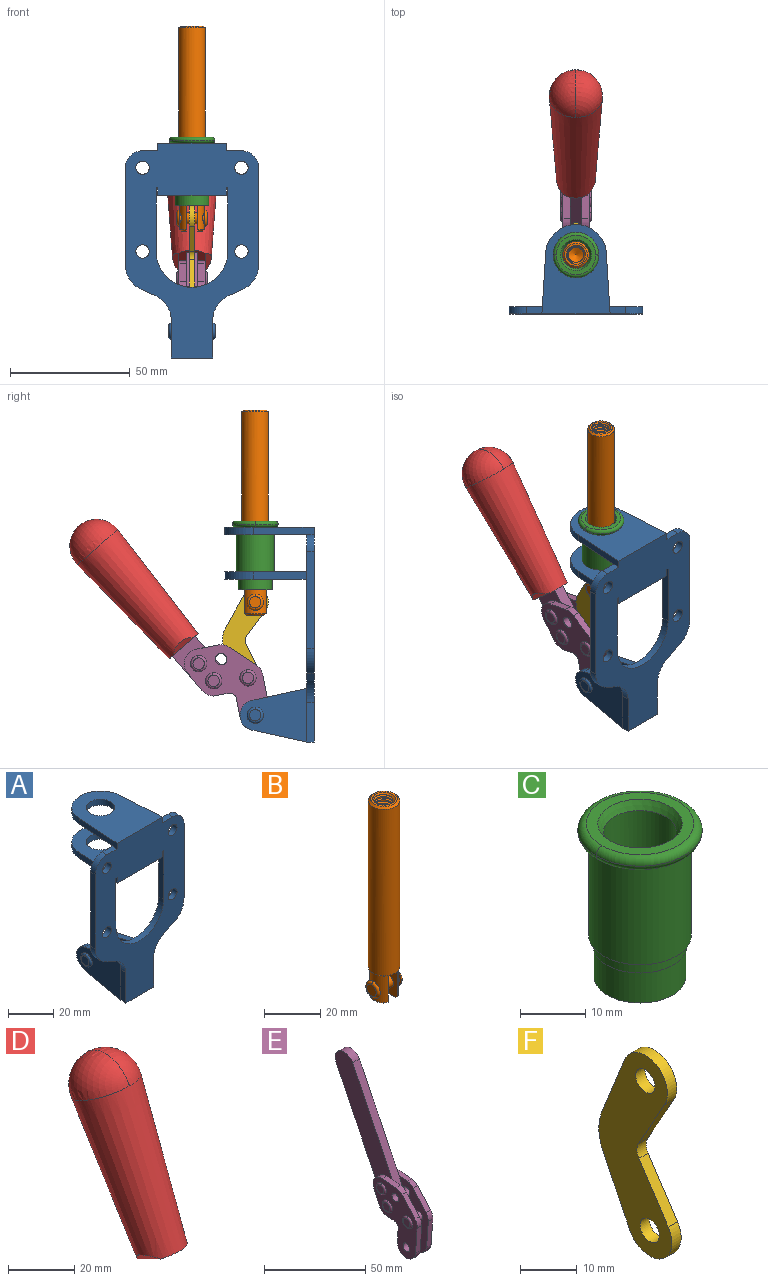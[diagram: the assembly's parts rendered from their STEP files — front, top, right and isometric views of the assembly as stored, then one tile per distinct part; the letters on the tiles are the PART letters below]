
ASSEMBLY  parts=6 mates=6
PART A: 55 faces, bbox 55.7x37.4x89.8 mm
  f0: torus R=2.41mm, axis (-1,0,0), area 15mm2, adj f11,f15,f25
  f1: torus R=2.41mm, axis (-1,0,0), area 15mm2, adj f10,f12,f22
  f2: cylinder r=2.78mm len=5.56mm, axis (0,-1,0), area 54.2mm2, adj f30,f54
  f3: cylinder r=14.99mm len=29.97mm, axis (0,-1,0), area 145.9mm2, adj f30,f49,f53,f54
  f4: cylinder r=2.78mm len=5.56mm, axis (0,-1,0), area 54.2mm2, adj f30,f54
  f5: cylinder r=2.78mm len=5.56mm, axis (0,-1,0), area 54.2mm2, adj f30,f54
  f6: cylinder r=2.78mm len=5.56mm, axis (0,-1,0), area 54.2mm2, adj f30,f54
  f7: cylinder r=6.35mm len=12.7mm, axis (0,0,1), area 123.6mm2, adj f27,f51
  f8: cylinder r=6.35mm len=12.7mm, axis (0,0,-1), area 124.7mm2, adj f21,f35
  f9: cylinder r=2.41mm len=11.18mm, axis (-1,0,0), area 169.4mm2, adj f16,f19
  f10: plane 4.83x4.83mm, normal (1,0,0), area 18.3mm2, adj f1,f12
  f11: plane 4.83x4.83mm, normal (-1,0,0), area 18.3mm2, adj f0,f15
  f12: torus R=2.41mm, axis (-1,0,0), area 15mm2, adj f1,f10,f22
  f13: cylinder r=6.35mm len=12.41mm, axis (1,0,0), area 53.4mm2, adj f18,f19,f22,f23
  f14: cylinder r=6.35mm len=12.41mm, axis (-1,0,0), area 53.4mm2, adj f16,f17,f24,f25
  f15: torus R=2.41mm, axis (-1,0,0), area 15mm2, adj f0,f11,f25
  f16: plane 27.86x22.35mm, normal (1,0,0), area 425.4mm2, adj f9,f14,f17,f24,f30
  f17: plane 22.86x4.97mm, normal (0,0.21,0.98), area 72.5mm2, adj f14,f16,f25,f30
  f18: plane 22.86x4.97mm, normal (0,0.21,0.98), area 72.5mm2, adj f13,f19,f22,f30
  f19: plane 27.86x22.35mm, normal (-1,0,0), area 425.4mm2, adj f9,f13,f18,f23,f30
  f20: cylinder r=12.7mm len=25.35mm, axis (0,0,-1), area 119.8mm2, adj f21,f34,f35,f36
  f21: plane 34.21x28.07mm, normal (0,0,-1), area 702.4mm2, adj f8,f20,f30,f34,f36
  f22: plane 27.96x22.45mm, normal (1,0,0), area 407.2mm2, adj f1,f12,f13,f18,f23,f30,f42,f43
  f23: plane 22.86x4.97mm, normal (0,0.21,-0.98), area 72.5mm2, adj f13,f19,f22,f44
  f24: plane 22.86x4.97mm, normal (0,0.21,-0.98), area 72.5mm2, adj f14,f16,f25,f44
  f25: plane 27.86x22.35mm, normal (-1,0,0), area 407.1mm2, adj f0,f14,f15,f17,f24,f30,f45,f46
  f26: plane 3.1x0.95mm, normal (0,0,-1), area 2.7mm2, adj f30,f49,f50,f54
  f27: plane 34.21x28.07mm, normal (0,0,1), area 702.4mm2, adj f7,f28,f30,f50,f52
  f28: cylinder r=12.7mm len=25.35mm, axis (0,0,1), area 118.8mm2, adj f27,f50,f51,f52
  f29: plane 3.1x0.95mm, normal (0,0,-1), area 2.7mm2, adj f30,f52,f53,f54
  f30: plane 86.54x55.63mm, normal (0,1,0), area 2362.9mm2, adj f2,f3,f4,f5,f6,f16,f17,f18
  f31: plane 40.56x3.1mm, normal (-1,0,0), area 125.7mm2, adj f30,f32,f48,f54
  f32: cylinder r=7.11mm len=7.11mm, axis (0,-1,0), area 34.6mm2, adj f30,f31,f33,f54
  f33: plane 6.67x3.1mm, normal (0,0,1), area 20.4mm2, adj f30,f32,f34,f54
  f34: plane 25.39x3.13mm, normal (-1,0.06,0), area 79.5mm2, adj f20,f21,f33,f35,f54
  f35: plane 37.31x28.45mm, normal (0,0,1), area 789.9mm2, adj f8,f20,f34,f36,f54
  f36: plane 25.39x3.13mm, normal (1,0.06,0), area 79.5mm2, adj f20,f21,f35,f37,f54
  f37: plane 6.67x3.1mm, normal (0,0,1), area 20.4mm2, adj f30,f36,f38,f54
  f38: cylinder r=7.11mm len=7.11mm, axis (0,-1,0), area 34.6mm2, adj f30,f37,f39,f54
  f39: plane 40.56x3.1mm, normal (1,0,0), area 125.7mm2, adj f30,f38,f40,f54
  f40: cylinder r=11.18mm len=10.16mm, axis (0,-1,0), area 39.5mm2, adj f30,f39,f41,f54
  f41: plane 6.09x3.1mm, normal (0.42,0,-0.91), area 20.8mm2, adj f30,f40,f42,f54
  f42: cylinder r=11.18mm len=9.41mm, axis (0,-1,0), area 37.2mm2, adj f22,f30,f41,f43,f54
  f43: plane 16.5x3.1mm, normal (1,0,0), area 51.1mm2, adj f22,f42,f44,f54
  f44: plane 17.37x3.1mm, normal (0,0,-1), area 53.8mm2, adj f23,f24,f30,f43,f45,f54
  f45: plane 16.5x3.1mm, normal (-1,0,0), area 51.1mm2, adj f25,f44,f46,f54
  f46: cylinder r=11.18mm len=9.41mm, axis (0,-1,0), area 37.2mm2, adj f25,f30,f45,f47,f54
  f47: plane 6.09x3.1mm, normal (-0.42,0,-0.91), area 20.8mm2, adj f30,f46,f48,f54
  f48: cylinder r=11.18mm len=10.16mm, axis (0,-1,0), area 39.5mm2, adj f30,f31,f47,f54
  f49: plane 26.54x3.1mm, normal (-1,0,0), area 82.3mm2, adj f3,f26,f30,f54
  f50: plane 25.39x3.1mm, normal (1,0.06,0), area 78.8mm2, adj f26,f27,f28,f51,f54
  f51: plane 37.31x28.45mm, normal (0,0,-1), area 789.9mm2, adj f7,f28,f50,f52,f54
  f52: plane 25.39x3.1mm, normal (-1,0.06,0), area 78.8mm2, adj f27,f28,f29,f51,f54
  f53: plane 26.54x3.1mm, normal (1,0,0), area 82.3mm2, adj f3,f29,f30,f54
  f54: plane 89.66x55.63mm, normal (0,-1,0), area 2678.5mm2, adj f2,f3,f4,f5,f6,f26,f29,f31
PART B: 48 faces, bbox 12.6x11.1x86.1 mm
  f0: torus R=2.41mm, axis (-1,0,0), area 15mm2, adj f30,f32,f34
  f1: torus R=2.41mm, axis (-1,0,0), area 15mm2, adj f29,f31,f33
  f2: cylinder r=5.54mm len=72.39mm, axis (0,0,1), area 2518.5mm2, adj f3,f4,f42,f43
  f3: cone r=5.54mm half-angle=45deg, axis (0,0,1), area 7.6mm2, adj f2,f5,f41
  f4: cone r=5.54mm half-angle=45deg, axis (0,0,-1), area 34.9mm2, adj f2,f39
  f5: cylinder r=5.08mm len=11.48mm, axis (0,0,1), area 108.3mm2, adj f3,f7,f8,f41
  f6: cylinder r=2.41mm len=4.83mm, axis (-1,0,0), area 71.2mm2, adj f40,f41
  f7: cylinder r=2.41mm len=4.83mm, axis (-1,0,0), area 7.6mm2, adj f5,f34
  f8: cone r=5.08mm half-angle=45deg, axis (0,0,1), area 10.6mm2, adj f5,f37,f41
  f9: cone r=3.98mm half-angle=45deg, axis (0,0,1), area 17.6mm2, adj f27,f39,f45,f46,f47
  f10: cylinder r=2.41mm len=4.83mm, axis (-1,0,0), area 7.6mm2, adj f33,f38
  f11: cylinder r=3.2mm len=6.4mm, axis (0,0,1), area 78.4mm2, adj f12,f28,f44,f45,f47
  f12: cylinder r=3.2mm len=6.4mm, axis (0,0,1), area 10.5mm2, adj f11,f13,f45,f47
  f13: cylinder r=3.2mm len=6.4mm, axis (0,0,1), area 10.5mm2, adj f12,f14,f45,f47
  f14: cylinder r=3.2mm len=6.4mm, axis (0,0,1), area 10.5mm2, adj f13,f15,f45,f47
  f15: cylinder r=3.2mm len=6.4mm, axis (0,0,1), area 10.5mm2, adj f14,f16,f45,f47
  f16: cylinder r=3.2mm len=6.4mm, axis (0,0,1), area 10.5mm2, adj f15,f17,f45,f47
  f17: cylinder r=3.2mm len=6.4mm, axis (0,0,1), area 10.5mm2, adj f16,f18,f45,f47
  f18: cylinder r=3.2mm len=6.4mm, axis (0,0,1), area 10.5mm2, adj f17,f19,f45,f47
  f19: cylinder r=3.2mm len=6.4mm, axis (0,0,1), area 10.5mm2, adj f18,f20,f45,f47
  f20: cylinder r=3.2mm len=6.4mm, axis (0,0,1), area 10.5mm2, adj f19,f21,f45,f47
  f21: cylinder r=3.2mm len=6.4mm, axis (0,0,1), area 10.5mm2, adj f20,f22,f45,f47
  f22: cylinder r=3.2mm len=6.4mm, axis (0,0,1), area 10.5mm2, adj f21,f23,f45,f47
  f23: cylinder r=3.2mm len=6.4mm, axis (0,0,1), area 10.5mm2, adj f22,f24,f45,f47
  f24: cylinder r=3.2mm len=6.4mm, axis (0,0,1), area 10.5mm2, adj f23,f25,f45,f47
  f25: cylinder r=3.2mm len=6.4mm, axis (0,0,1), area 10.5mm2, adj f24,f26,f45,f47
  f26: cylinder r=3.2mm len=6.4mm, axis (0,0,1), area 10.5mm2, adj f25,f27,f45,f47
  f27: cylinder r=3.2mm len=6.4mm, axis (0,0,1), area 7.4mm2, adj f9,f26,f45,f47
  f28: cone r=3.2mm half-angle=60deg, axis (0,0,1), area 37.2mm2, adj f11
  f29: plane 4.83x4.83mm, normal (-1,0,0), area 18.3mm2, adj f1,f31
  f30: plane 4.83x4.83mm, normal (1,0,0), area 18.3mm2, adj f0,f32
  f31: torus R=2.41mm, axis (-1,0,0), area 15mm2, adj f1,f29,f33
  f32: torus R=2.41mm, axis (-1,0,0), area 15mm2, adj f0,f30,f34
  f33: plane 6.83x6.83mm, normal (1,0,0), area 18.3mm2, adj f1,f10,f31
  f34: plane 6.83x6.83mm, normal (-1,0,0), area 18.3mm2, adj f0,f7,f32
  f35: cone r=5.08mm half-angle=45deg, axis (0,0,1), area 10.6mm2, adj f36,f38,f40
  f36: plane 7.25x1.97mm, normal (0,0,-1), area 10mm2, adj f35,f40
  f37: plane 7.25x1.97mm, normal (0,0,-1), area 10mm2, adj f8,f41
  f38: cylinder r=5.08mm len=11.48mm, axis (0,0,1), area 108.3mm2, adj f10,f35,f40,f42
  f39: plane 9.55x9.55mm, normal (0,0,1), area 22mm2, adj f4,f9
  f40: plane 12.76x10.09mm, normal (1,0,0), area 95.7mm2, adj f6,f35,f36,f38,f42,f43
  f41: plane 12.76x10.09mm, normal (-1,0,0), area 95.7mm2, adj f3,f5,f6,f8,f37,f43
  f42: cone r=5.54mm half-angle=45deg, axis (0,0,1), area 7.6mm2, adj f2,f38,f40
  f43: plane 11.07x4.7mm, normal (0,0,-1), area 50.4mm2, adj f2,f40,f41
  f44: plane 0.89x0.62mm, normal (-1,0,0), area 0.3mm2, adj f11,f45,f46,f47
  f45: bspline ~24.8x7.63mm, area 266.6mm2, adj f9,f11,f12,f13,f14,f15,f16,f17
  f46: bspline ~24.87x7.63mm, area 73.6mm2, adj f9,f44,f45,f47
  f47: bspline ~24.98x7.63mm, area 272.5mm2, adj f9,f11,f12,f13,f14,f15,f16,f17
PART C: 15 faces, bbox 20.6x20.6x28.7 mm
  f0: torus R=8.26mm, axis (0,0,1), area 56.8mm2, adj f1,f10,f12
  f1: torus R=8.26mm, axis (0,0,1), area 56.8mm2, adj f0,f6,f13
  f2: cylinder r=5.59mm len=25.91mm, axis (0,0,1), area 909.6mm2, adj f3,f4
  f3: cone r=6.86mm half-angle=45deg, axis (0,0,-1), area 70.2mm2, adj f2,f14
  f4: cone r=6.47mm half-angle=30deg, axis (0,0,1), area 66.7mm2, adj f2,f13
  f5: cylinder r=7.04mm len=14.07mm, axis (0,0,1), area 252.6mm2, adj f11,f14
  f6: torus R=8.26mm, axis (0,0,1), area 56.8mm2, adj f1,f12,f13
  f7: cylinder r=7.16mm len=14.33mm, axis (0,0,1), area 91.5mm2, adj f9,f11
  f8: cylinder r=7.86mm len=18.42mm, axis (0,0,1), area 909.6mm2, adj f9,f10
  f9: plane 15.72x15.72mm, normal (0,0,-1), area 33mm2, adj f7,f8
  f10: plane 16.51x16.51mm, normal (0,0,-1), area 19.9mm2, adj f0,f8,f12
  f11: plane 14.33x14.33mm, normal (0,0,-1), area 5.7mm2, adj f5,f7
  f12: torus R=8.26mm, axis (0,0,1), area 56.8mm2, adj f0,f6,f10
  f13: plane 16.51x16.51mm, normal (0,0,1), area 82.7mm2, adj f1,f4,f6
  f14: plane 14.07x14.07mm, normal (0,0,-1), area 7.8mm2, adj f3,f5
PART D: 11 faces, bbox 22.3x42.6x64.5 mm
  f0: sphere r=11.13mm, area 411.4mm2, adj f1,f8
  f1: cone r=11.11mm half-angle=3.3deg, axis (0,0.44,0.9), area 3251.8mm2, adj f0,f7,f8,f9,f10
  f2: cylinder r=6.16mm len=11.7mm, axis (1,0,0), area 89.5mm2, adj f3,f4,f5,f6
  f3: plane 60.23x36.75mm, normal (-1,0,0), area 763.6mm2, adj f2,f4,f6,f10
  f4: plane 51.37x25.05mm, normal (0,0.9,-0.44), area 264.2mm2, adj f2,f3,f5,f10
  f5: plane 60.23x36.75mm, normal (1,0,0), area 763.6mm2, adj f2,f4,f6,f10
  f6: plane 51.37x25.05mm, normal (0,-0.9,0.44), area 264.2mm2, adj f2,f3,f5,f10
  f7: plane 9.95x5.95mm, normal (0.71,-0.31,-0.64), area 25.8mm2, adj f1,f10
  f8: sphere r=11.13mm, area 411.4mm2, adj f0,f1
  f9: plane 9.95x5.95mm, normal (-0.71,-0.31,-0.64), area 25.8mm2, adj f1,f10
  f10: plane 14.27x11.38mm, normal (0,-0.44,-0.9), area 106.7mm2, adj f1,f3,f4,f5,f6,f7,f9
PART E: 59 faces, bbox 12.9x60.2x99.6 mm
  f0: torus R=2.39mm, axis (-1,0,0), area 14.9mm2, adj f20,f43,f51
  f1: torus R=2.39mm, axis (-1,0,0), area 14.9mm2, adj f19,f42,f51
  f2: torus R=2.39mm, axis (-1,0,0), area 14.9mm2, adj f18,f35,f51
  f3: torus R=2.39mm, axis (-1,0,0), area 14.9mm2, adj f14,f17,f23
  f4: torus R=2.39mm, axis (-1,0,0), area 14.9mm2, adj f13,f16,f23
  f5: torus R=2.39mm, axis (-1,0,0), area 14.9mm2, adj f12,f15,f23
  f6: cylinder r=2.39mm len=4.78mm, axis (1,0,0), area 46.5mm2, adj f48,f50,f51
  f7: cylinder r=2.39mm len=4.78mm, axis (1,0,0), area 46.5mm2, adj f50,f51
  f8: cylinder r=6.35mm len=12.68mm, axis (1,0,0), area 61.8mm2, adj f38,f39,f50,f51
  f9: cylinder r=2.39mm len=4.78mm, axis (-1,0,0), area 70.5mm2, adj f46,f50
  f10: cylinder r=2.39mm len=4.78mm, axis (-1,0,0), area 46.5mm2, adj f23,f45,f46
  f11: cylinder r=2.39mm len=4.78mm, axis (-1,0,0), area 46.5mm2, adj f23,f46
  f12: plane 4.78x4.78mm, normal (1,0,0), area 17.9mm2, adj f5,f15
  f13: plane 4.78x4.78mm, normal (1,0,0), area 17.9mm2, adj f4,f16
  f14: plane 4.78x4.78mm, normal (1,0,0), area 17.9mm2, adj f3,f17
  f15: torus R=2.39mm, axis (-1,0,0), area 14.9mm2, adj f5,f12,f23
  f16: torus R=2.39mm, axis (-1,0,0), area 14.9mm2, adj f4,f13,f23
  f17: torus R=2.39mm, axis (-1,0,0), area 14.9mm2, adj f3,f14,f23
  f18: plane 4.78x4.78mm, normal (-1,0,0), area 17.9mm2, adj f2,f35
  f19: plane 4.78x4.78mm, normal (-1,0,0), area 17.9mm2, adj f1,f42
  f20: plane 4.78x4.78mm, normal (-1,0,0), area 17.9mm2, adj f0,f43
  f21: plane 2.26x0.2mm, normal (1,0,0), area 0.2mm2, adj f31,f44
  f22: plane 2.26x0.2mm, normal (-1,0,0), area 0.2mm2, adj f41,f44
  f23: plane 39.37x30.77mm, normal (1,0,0), area 565.5mm2, adj f3,f4,f5,f10,f11,f15,f16,f17
  f24: cylinder r=6.1mm len=4.15mm, axis (-1,0,0), area 14.7mm2, adj f23,f25,f32,f46
  f25: plane 10.25x9.01mm, normal (0,-0.75,0.66), area 42.3mm2, adj f23,f24,f26,f46
  f26: cylinder r=6.35mm len=4.64mm, axis (-1,0,0), area 15.6mm2, adj f23,f25,f27,f46
  f27: plane 15.84x3.1mm, normal (0,-1,-0.07), area 49.2mm2, adj f23,f26,f28,f46
  f28: cylinder r=6.35mm len=12.68mm, axis (-1,0,0), area 61.8mm2, adj f23,f27,f29,f46
  f29: plane 8.11x3.1mm, normal (0,1,0.07), area 25.2mm2, adj f23,f28,f30,f46
  f30: cylinder r=3.05mm len=3.25mm, axis (-1,0,0), area 14.8mm2, adj f23,f29,f31,f46
  f31: plane 5.99x3.1mm, normal (0,0.07,-1), area 18.6mm2, adj f21,f23,f30,f44,f46
  f32: plane 9.5x3.1mm, normal (0,-0.07,1), area 29.5mm2, adj f23,f24,f33,f46,f47
  f33: cylinder r=6.1mm len=8.63mm, axis (-1,0,0), area 39.1mm2, adj f23,f32,f34,f47
  f34: plane 8.65x3.96mm, normal (0,0.91,-0.42), area 29.5mm2, adj f23,f33,f44,f47
  f35: torus R=2.39mm, axis (-1,0,0), area 14.9mm2, adj f2,f18,f51
  f36: plane 10.25x9.01mm, normal (0,-0.75,0.66), area 42.3mm2, adj f37,f49,f50,f51
  f37: cylinder r=6.35mm len=4.64mm, axis (1,0,0), area 15.6mm2, adj f36,f38,f50,f51
  f38: plane 15.84x3.1mm, normal (0,-1,-0.07), area 49.2mm2, adj f8,f37,f50,f51
  f39: plane 8.11x3.1mm, normal (0,1,0.07), area 25.2mm2, adj f8,f40,f50,f51
  f40: cylinder r=3.05mm len=3.25mm, axis (1,0,0), area 14.8mm2, adj f39,f41,f50,f51
  f41: plane 5.99x3.1mm, normal (0,0.07,-1), area 18.6mm2, adj f22,f40,f44,f50,f51
  f42: torus R=2.39mm, axis (-1,0,0), area 14.9mm2, adj f1,f19,f51
  f43: torus R=2.39mm, axis (-1,0,0), area 14.9mm2, adj f0,f20,f51
  f44: cylinder r=6.35mm len=12.12mm, axis (-1,0,0), area 128.9mm2, adj f21,f22,f23,f31,f34,f41,f46,f47
  f45: plane 2.65x1.35mm, normal (1,0,0), area 1mm2, adj f10,f55
  f46: plane 39.08x20.42mm, normal (-1,0,0), area 412.5mm2, adj f9,f10,f11,f24,f25,f26,f27,f28
  f47: plane 77.62x39.82mm, normal (1,0,0), area 850mm2, adj f32,f33,f34,f44,f53,f54,f55
  f48: plane 2.65x1.35mm, normal (-1,0,0), area 1mm2, adj f6,f55
  f49: cylinder r=6.1mm len=4.15mm, axis (1,0,0), area 14.7mm2, adj f36,f50,f51,f56
  f50: plane 39.08x20.42mm, normal (1,0,0), area 412.5mm2, adj f6,f7,f8,f9,f36,f37,f38,f39
  f51: plane 39.37x30.77mm, normal (-1,0,0), area 565.5mm2, adj f0,f1,f2,f6,f7,f8,f35,f36
  f52: plane 8.65x3.96mm, normal (0,0.91,-0.42), area 29.5mm2, adj f44,f51,f57,f58
  f53: plane 68.49x33.4mm, normal (0,0.9,-0.44), area 358.1mm2, adj f44,f47,f54,f58
  f54: cylinder r=6.35mm len=12.06mm, axis (1,0,0), area 93.7mm2, adj f47,f53,f55,f58
  f55: plane 68.49x33.4mm, normal (0,-0.9,0.44), area 358.1mm2, adj f44,f45,f46,f47,f48,f50,f54,f58
  f56: plane 9.5x3.1mm, normal (0,-0.07,1), area 29.5mm2, adj f49,f50,f51,f57,f58
  f57: cylinder r=6.1mm len=8.63mm, axis (1,0,0), area 39.1mm2, adj f51,f52,f56,f58
  f58: plane 77.62x39.82mm, normal (-1,0,0), area 850mm2, adj f44,f52,f53,f54,f55,f56,f57
PART F: 12 faces, bbox 2.3x18.2x42.8 mm
  f0: cylinder r=2.4mm len=4.8mm, axis (1,0,0), area 34.9mm2, adj f4,f11
  f1: cylinder r=10.41mm len=8.47mm, axis (1,0,0), area 20.2mm2, adj f4,f9,f10,f11
  f2: cylinder r=3.05mm len=3.16mm, axis (1,0,0), area 7.7mm2, adj f4,f6,f7,f11
  f3: cylinder r=2.4mm len=4.8mm, axis (1,0,0), area 34.9mm2, adj f4,f11
  f4: plane 42.81x18.23mm, normal (-1,0,0), area 414.1mm2, adj f0,f1,f2,f3,f5,f6,f7,f8
  f5: cylinder r=5.54mm len=10.67mm, axis (1,0,0), area 41.8mm2, adj f4,f6,f10,f11
  f6: plane 11.66x6.53mm, normal (0,-0.87,-0.49), area 30.9mm2, adj f2,f4,f5,f11
  f7: plane 11.17x7.33mm, normal (0,-0.84,0.55), area 30.9mm2, adj f2,f4,f8,f11
  f8: cylinder r=5.54mm len=10.51mm, axis (1,0,0), area 41.8mm2, adj f4,f7,f9,f11
  f9: plane 13.67x6.67mm, normal (0,0.9,-0.44), area 35.1mm2, adj f1,f4,f8,f11
  f10: plane 14.1x5.7mm, normal (0,0.93,0.37), area 35.1mm2, adj f1,f4,f5,f11
  f11: plane 42.81x18.23mm, normal (1,0,0), area 414.1mm2, adj f0,f1,f2,f3,f5,f6,f7,f8
PLACE A rot(axis=(0,0,-1),0deg) t=(0,0,-9.43)mm fixed
PLACE B rot(axis=(0,0,-1),0deg) t=(0,0,-9.81)mm
PLACE C rot(axis=(0,0,-1),0deg) t=(0,0,-9.43)mm
PLACE D rot(axis=(-1,0,0),15deg) t=(-0.04,9.14,-4.15)mm
PLACE E rot(axis=(-1,0,0),15deg) t=(0,9.14,-4.15)mm
PLACE F rot(axis=(1,0,0),7.5deg) t=(0,2.22,-12.88)mm
MATE revolute F.f3 <-> E.f4  axis (1,0,0) through (0,27.64,-25.94)mm
MATE fastened A.f7 <-> C.f0  axis (0,0,1) through (0,24.61,36.96)mm
MATE revolute A.f0 <-> E.f7  axis (-1,0,0) through (0,24.61,-41.52)mm
MATE fastened D.f2 <-> E.f54  axis (1,0,0) through (-2.35,91.94,30.37)mm
MATE slider B.f2 <-> A.f7  axis (0,0,1) through (0,24.61,48.97)mm
MATE revolute B.f6 <-> F.f5  axis (-1,0,0) through (0,24.61,5.67)mm
